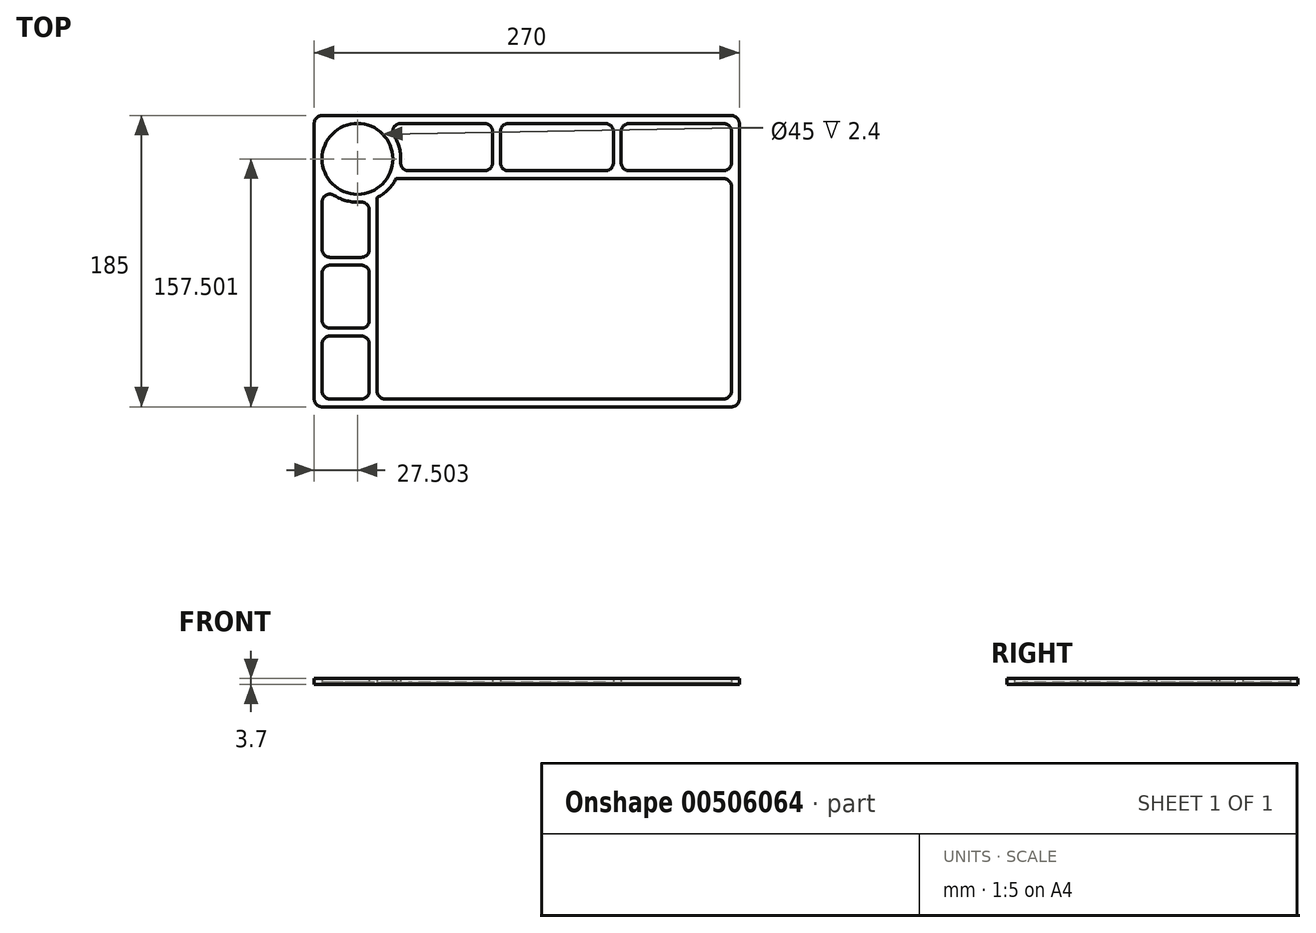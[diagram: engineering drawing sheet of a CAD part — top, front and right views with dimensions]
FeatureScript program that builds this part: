
annotation { "Feature Type Name" : "Feature", "Feature Type Description" : "" }
export const myFeature = defineFeature(function(context is Context, id is Id, definition is map)
    precondition{}
    {
        {
            var Q0;
            Q0=qCreatedBy(makeId("Top.planeOp"),FACE);
            var sketch = newSketch(context, id + "F0", { "sketchPlane" : qUnion([Q0])});
            skLineSegment(sketch, "E0.bottom", {"start": v(-130.88, 121.5) * mm, "end": v(129.12, 121.5) * mm});
            skLineSegment(sketch, "E0.top", {"start": v(-130.88, -63.5) * mm, "end": v(129.12, -63.5) * mm});
            skLineSegment(sketch, "E0.left", {"start": v(-135.88, 116.5) * mm, "end": v(-135.88, -58.5) * mm});
            skLineSegment(sketch, "E0.right", {"start": v(134.12, 116.5) * mm, "end": v(134.12, -58.5) * mm});
            skCircle(sketch, "E1", {"center": v(-108.38, 94) * mm, "radius": 22.5 * mm});
            skPoint(sketch, "E2.visualSharp", {"position": v(134.12, 121.5) * mm});
            skArc(sketch, "E2.filletArc", {"start": v(134.12, 116.5) * mm, "mid": v(132.66, 120.03) * mm, "end": v(129.12, 121.5) * mm});
            skPoint(sketch, "E3.visualSharp", {"position": v(-135.88, 121.5) * mm});
            skArc(sketch, "E3.filletArc", {"start": v(-130.88, 121.5) * mm, "mid": v(-134.41, 120.03) * mm, "end": v(-135.88, 116.5) * mm});
            skPoint(sketch, "E4.visualSharp", {"position": v(-135.88, -63.5) * mm});
            skArc(sketch, "E4.filletArc", {"start": v(-135.88, -58.5) * mm, "mid": v(-134.41, -62.04) * mm, "end": v(-130.88, -63.5) * mm});
            skPoint(sketch, "E5.visualSharp", {"position": v(134.12, -63.5) * mm});
            skArc(sketch, "E5.filletArc", {"start": v(129.12, -63.5) * mm, "mid": v(132.66, -62.04) * mm, "end": v(134.12, -58.5) * mm});
            skLineSegment(sketch, "E6", {"start": v(129.12, -58.5) * mm, "end": v(-95.88, -58.5) * mm, "construction": true});
            skArc(sketch, "E7", {"start": v(-81.92, 86.5) * mm, "mid": v(-82.46, 103.19) * mm, "end": v(-92.57, 116.5) * mm});
            skLineSegment(sketch, "E8", {"start": v(-92.57, 116.5) * mm, "end": v(-22.57, 116.5) * mm});
            skLineSegment(sketch, "E9", {"start": v(-22.57, 116.5) * mm, "end": v(-22.57, 86.5) * mm});
            skLineSegment(sketch, "E10", {"start": v(-22.57, 86.5) * mm, "end": v(-81.92, 86.5) * mm});
            skLineSegment(sketch, "E11.bottom", {"start": v(-23.62, 116.5) * mm, "end": v(-22.57, 116.5) * mm});
            skLineSegment(sketch, "E11.top", {"start": v(-23.62, 86.5) * mm, "end": v(-22.57, 86.5) * mm});
            skLineSegment(sketch, "E12", {"start": v(12.15, 86.5) * mm, "end": v(54.12, 86.5) * mm});
            skLineSegment(sketch, "E13", {"start": v(129.12, 86.5) * mm, "end": v(129.12, 116.5) * mm});
            skLineSegment(sketch, "E14", {"start": v(129.12, 116.5) * mm, "end": v(59.12, 116.5) * mm});
            skLineSegment(sketch, "E15", {"start": v(59.12, 116.5) * mm, "end": v(59.12, 86.5) * mm});
            skLineSegment(sketch, "E16", {"start": v(129.12, 116.5) * mm, "end": v(129.12, 86.5) * mm, "construction": true});
            skLineSegment(sketch, "E17", {"start": v(-83.88, 81.5) * mm, "end": v(129.12, 81.5) * mm});
            skLineSegment(sketch, "E18", {"start": v(129.12, 81.5) * mm, "end": v(129.12, -58.5) * mm});
            skLineSegment(sketch, "E19", {"start": v(-95.88, -58.5) * mm, "end": v(-95.88, 69.5) * mm});
            skArc(sketch, "E20.trimOffspring", {"start": v(-130.88, 78.18) * mm, "mid": v(-117.57, 68.07) * mm, "end": v(-100.88, 67.53) * mm});
            skLineSegment(sketch, "E21.trimOffspring", {"start": v(-92.57, 116.5) * mm, "end": v(-22.57, 116.5) * mm, "construction": true});
            skLineSegment(sketch, "E22.trimOffspring", {"start": v(-81.92, 86.5) * mm, "end": v(-22.57, 86.5) * mm, "construction": true});
            skLineSegment(sketch, "E23.trimOffspring", {"start": v(-23.62, 116.5) * mm, "end": v(-22.57, 116.5) * mm, "construction": true});
            skLineSegment(sketch, "E24.trimOffspring", {"start": v(-23.62, 86.5) * mm, "end": v(-22.57, 86.5) * mm, "construction": true});
            skLineSegment(sketch, "E25.trimOffspring", {"start": v(-83.88, 81.5) * mm, "end": v(129.12, 81.5) * mm, "construction": true});
            skLineSegment(sketch, "E26.trimOffspring", {"start": v(-95.88, 69.5) * mm, "end": v(-95.88, -58.5) * mm, "construction": true});
            skLineSegment(sketch, "E27.trimOffspring", {"start": v(-100.88, 67.53) * mm, "end": v(-100.88, 31.5) * mm, "construction": true});
            skLineSegment(sketch, "E28", {"start": v(-130.88, 78.18) * mm, "end": v(-130.88, 31.5) * mm});
            skLineSegment(sketch, "E29", {"start": v(-100.88, -58.5) * mm, "end": v(-100.88, -18.5) * mm});
            skArc(sketch, "E30.trimOffspring", {"start": v(-95.88, 69.5) * mm, "mid": v(-88.93, 74.55) * mm, "end": v(-83.88, 81.5) * mm});
            skLineSegment(sketch, "E31.trimOffspring", {"start": v(-130.88, 78.18) * mm, "end": v(-130.88, 31.5) * mm, "construction": true});
            skLineSegment(sketch, "E32", {"start": v(-95.88, -58.5) * mm, "end": v(129.12, -58.5) * mm});
            skLineSegment(sketch, "E33", {"start": v(-130.88, -58.5) * mm, "end": v(-100.88, -58.5) * mm});
            skPoint(sketch, "E34.end.orphan", {"position": v(12.15, 86.5) * mm});
            skLineSegment(sketch, "E35.trimOffspring", {"start": v(12.15, 86.5) * mm, "end": v(54.12, 86.5) * mm, "construction": true});
            skLineSegment(sketch, "E36", {"start": v(-17.57, 116.5) * mm, "end": v(-17.57, 86.5) * mm});
            skLineSegment(sketch, "E37", {"start": v(54.12, 116.5) * mm, "end": v(54.12, 86.5) * mm});
            skLineSegment(sketch, "E38.trimOffspring", {"start": v(-17.57, 116.5) * mm, "end": v(54.12, 116.5) * mm, "construction": true});
            skLineSegment(sketch, "E39.trimOffspring", {"start": v(59.12, 86.5) * mm, "end": v(129.12, 86.5) * mm, "construction": true});
            skLineSegment(sketch, "E40.trimOffspring", {"start": v(59.12, 116.5) * mm, "end": v(129.12, 116.5) * mm, "construction": true});
            skPoint(sketch, "E41.orphan", {"position": v(-20.88, 116.5) * mm});
            skLineSegment(sketch, "E42.trimOffspring", {"start": v(54.12, 116.5) * mm, "end": v(-17.57, 116.5) * mm});
            skLineSegment(sketch, "E43.trimOffspring", {"start": v(59.12, 86.5) * mm, "end": v(129.12, 86.5) * mm});
            skPoint(sketch, "E44.orphan", {"position": v(-20.88, 86.5) * mm});
            skLineSegment(sketch, "E45", {"start": v(12.15, 86.5) * mm, "end": v(-17.57, 86.5) * mm});
            skLineSegment(sketch, "E46", {"start": v(-130.88, -18.5) * mm, "end": v(-100.88, -18.5) * mm});
            skLineSegment(sketch, "E47", {"start": v(-100.88, -13.5) * mm, "end": v(-130.88, -13.5) * mm});
            skLineSegment(sketch, "E48", {"start": v(-100.88, 26.5) * mm, "end": v(-130.88, 26.5) * mm});
            skLineSegment(sketch, "E49", {"start": v(-100.88, 31.5) * mm, "end": v(-130.88, 31.5) * mm});
            skLineSegment(sketch, "E50.trimOffspring", {"start": v(-130.88, 26.5) * mm, "end": v(-130.88, -13.5) * mm, "construction": true});
            skLineSegment(sketch, "E51.trimOffspring", {"start": v(-100.88, 26.5) * mm, "end": v(-100.88, -13.5) * mm, "construction": true});
            skLineSegment(sketch, "E52.trimOffspring", {"start": v(-100.88, -18.5) * mm, "end": v(-100.88, -58.5) * mm, "construction": true});
            skLineSegment(sketch, "E53.trimOffspring", {"start": v(-130.88, -18.5) * mm, "end": v(-130.88, -58.5) * mm, "construction": true});
            skLineSegment(sketch, "E54.trimOffspring", {"start": v(-100.88, -13.5) * mm, "end": v(-100.88, 26.5) * mm});
            skLineSegment(sketch, "E55.trimOffspring", {"start": v(-100.88, 31.5) * mm, "end": v(-100.88, 67.53) * mm});
            skLineSegment(sketch, "E56.trimOffspring", {"start": v(-130.88, 26.5) * mm, "end": v(-130.88, -13.5) * mm});
            skLineSegment(sketch, "E57.trimOffspring", {"start": v(-130.88, -18.5) * mm, "end": v(-130.88, -58.5) * mm});
            skPoint(sketch, "E58.orphan", {"position": v(-135.88, 86.5) * mm});
            skPoint(sketch, "E59.start.orphan", {"position": v(-135.88, 81.5) * mm});
            skPoint(sketch, "E60.orphan", {"position": v(-95.88, 121.5) * mm});
            skPoint(sketch, "E61.orphan", {"position": v(-100.88, 121.5) * mm});
            skPoint(sketch, "E62.orphan", {"position": v(129.12, 121.5) * mm});
            skLineSegment(sketch, "E63.trimOffspring", {"start": v(129.12, 81.5) * mm, "end": v(129.12, -58.5) * mm, "construction": true});
            skPoint(sketch, "E64.orphan", {"position": v(129.12, -63.5) * mm});
            skSolve(sketch);
        }
        {
            var Q0;
            Q0=makeQuery(id+"F0.imprint","IMPRINT",FACE,{"disambiguationData":[TD([[makeQuery(id+"F0.imprint","IMPRINT",EDGE,{"derivedFrom":sQuery(id+"F0.wireOp",EDGE,"E0.bottom")}),-1.0]])]});
            extrude(context, id + "F1", {"entities" : qUnion([Q0]), "depth" : 3.7 * mm, "offsetDistance" : 25 * mm});
        }
        {
            var Q0;
            Q0=makeQuery(id+"F0.imprint","IMPRINT",FACE,{"disambiguationData":[TD([[makeQuery(id+"F0.imprint","IMPRINT",EDGE,{"derivedFrom":sQuery(id+"F0.wireOp",EDGE,"E0.bottom")}),-1.0]])]});
            var Q1;
            Q1=makeQuery(id+"F0.imprint","IMPRINT",FACE,{"disambiguationData":[TD([[makeQuery(id+"F0.imprint","IMPRINT",EDGE,{"derivedFrom":sQuery(id+"F0.wireOp",EDGE,"E17")}),-1.0]])]});
            var Q2;
            Q2=makeQuery(id+"F0.imprint","IMPRINT",FACE,{"disambiguationData":[TD([[makeQuery(id+"F0.imprint","IMPRINT",EDGE,{"derivedFrom":sQuery(id+"F0.wireOp",EDGE,"E13")}),1.0]])]});
            var Q3;
            Q3=makeQuery(id+"F0.imprint","IMPRINT",FACE,{"disambiguationData":[TD([[makeQuery(id+"F0.imprint","IMPRINT",EDGE,{"derivedFrom":sQuery(id+"F0.wireOp",EDGE,"E12")}),1.0]])]});
            var Q4;
            Q4=makeQuery(id+"F0.imprint","IMPRINT",FACE,{"disambiguationData":[TD([[makeQuery(id+"F0.imprint","IMPRINT",EDGE,{"derivedFrom":sQuery(id+"F0.wireOp",EDGE,"E7")}),-1.0]])]});
            var Q5;
            Q5=makeQuery(id+"F0.imprint","IMPRINT",FACE,{"disambiguationData":[TD([[makeQuery(id+"F0.imprint","IMPRINT",EDGE,{"derivedFrom":sQuery(id+"F0.wireOp",EDGE,"E1")}),1.0]])]});
            var Q6;
            Q6=makeQuery(id+"F0.imprint","IMPRINT",FACE,{"disambiguationData":[TD([[makeQuery(id+"F0.imprint","IMPRINT",EDGE,{"derivedFrom":sQuery(id+"F0.wireOp",EDGE,"E20.trimOffspring")}),-1.0]])]});
            var Q7;
            Q7=makeQuery(id+"F0.imprint","IMPRINT",FACE,{"disambiguationData":[TD([[makeQuery(id+"F0.imprint","IMPRINT",EDGE,{"derivedFrom":sQuery(id+"F0.wireOp",EDGE,"E47")}),-1.0]])]});
            var Q8;
            Q8=makeQuery(id+"F0.imprint","IMPRINT",FACE,{"disambiguationData":[TD([[makeQuery(id+"F0.imprint","IMPRINT",EDGE,{"derivedFrom":sQuery(id+"F0.wireOp",EDGE,"E29")}),1.0]])]});
            extrude(context, id + "F2", {"entities" : qUnion([Q0, Q1, Q2, Q3, Q4, Q5, Q6, Q7, Q8]), "operationType" : NewBodyOperationType.ADD, "depth" : 1.3 * mm, "offsetDistance" : 25 * mm});
        }
        {
            var Q0;
            Q0=makeQuery(id+"F1.opExtrude","SWEPT_EDGE",EDGE,{"disambiguationData":[OSD([sQuery(id+"F0.wireOp",EDGE,"E14"),sQuery(id+"F0.wireOp",EDGE,"E15")])]});
            var Q1;
            Q1=makeQuery(id+"F1.opExtrude","SWEPT_EDGE",EDGE,{"disambiguationData":[OSD([sQuery(id+"F0.wireOp",EDGE,"E17"),sQuery(id+"F0.wireOp",EDGE,"E18")])]});
            var Q2;
            Q2=makeQuery(id+"F1.opExtrude","SWEPT_EDGE",EDGE,{"disambiguationData":[OSD([sQuery(id+"F0.wireOp",EDGE,"E13"),sQuery(id+"F0.wireOp",EDGE,"E14")])]});
            var Q3;
            Q3=makeQuery(id+"F1.opExtrude","SWEPT_EDGE",EDGE,{"disambiguationData":[OSD([sQuery(id+"F0.wireOp",EDGE,"E13"),sQuery(id+"F0.wireOp",EDGE,"E43.trimOffspring")])]});
            var Q4;
            Q4=makeQuery(id+"F1.opExtrude","SWEPT_EDGE",EDGE,{"disambiguationData":[OSD([sQuery(id+"F0.wireOp",EDGE,"E15"),sQuery(id+"F0.wireOp",EDGE,"E43.trimOffspring")])]});
            var Q5;
            Q5=makeQuery(id+"F1.opExtrude","SWEPT_EDGE",EDGE,{"disambiguationData":[OSD([sQuery(id+"F0.wireOp",EDGE,"E12"),sQuery(id+"F0.wireOp",EDGE,"E37")])]});
            var Q6;
            Q6=makeQuery(id+"F1.opExtrude","SWEPT_EDGE",EDGE,{"disambiguationData":[OSD([sQuery(id+"F0.wireOp",EDGE,"E37"),sQuery(id+"F0.wireOp",EDGE,"E42.trimOffspring")])]});
            var Q7;
            Q7=makeQuery(id+"F1.opExtrude","SWEPT_EDGE",EDGE,{"disambiguationData":[OSD([sQuery(id+"F0.wireOp",EDGE,"E36"),sQuery(id+"F0.wireOp",EDGE,"E45")])]});
            var Q8;
            Q8=makeQuery(id+"F1.opExtrude","SWEPT_EDGE",EDGE,{"disambiguationData":[OSD([sQuery(id+"F0.wireOp",EDGE,"E7"),sQuery(id+"F0.wireOp",EDGE,"E10")])]});
            var Q9;
            Q9=makeQuery(id+"F1.opExtrude","SWEPT_EDGE",EDGE,{"disambiguationData":[OSD([sQuery(id+"F0.wireOp",EDGE,"E47"),sQuery(id+"F0.wireOp",EDGE,"E56.trimOffspring")])]});
            var Q10;
            Q10=makeQuery(id+"F1.opExtrude","SWEPT_EDGE",EDGE,{"disambiguationData":[OSD([sQuery(id+"F0.wireOp",EDGE,"E48"),sQuery(id+"F0.wireOp",EDGE,"E54.trimOffspring")])]});
            var Q11;
            Q11=makeQuery(id+"F1.opExtrude","SWEPT_EDGE",EDGE,{"disambiguationData":[OSD([sQuery(id+"F0.wireOp",EDGE,"E20.trimOffspring"),sQuery(id+"F0.wireOp",EDGE,"E55.trimOffspring")])]});
            var Q12;
            Q12=makeQuery(id+"F1.opExtrude","SWEPT_EDGE",EDGE,{"disambiguationData":[OSD([sQuery(id+"F0.wireOp",EDGE,"E29"),sQuery(id+"F0.wireOp",EDGE,"E46")])]});
            var Q13;
            Q13=makeQuery(id+"F1.opExtrude","SWEPT_EDGE",EDGE,{"disambiguationData":[OSD([sQuery(id+"F0.wireOp",EDGE,"E48"),sQuery(id+"F0.wireOp",EDGE,"E56.trimOffspring")])]});
            var Q14;
            Q14=makeQuery(id+"F1.opExtrude","SWEPT_EDGE",EDGE,{"disambiguationData":[OSD([sQuery(id+"F0.wireOp",EDGE,"E20.trimOffspring"),sQuery(id+"F0.wireOp",EDGE,"E28")])]});
            var Q15;
            Q15=makeQuery(id+"F1.opExtrude","SWEPT_EDGE",EDGE,{"disambiguationData":[OSD([sQuery(id+"F0.wireOp",EDGE,"E7"),sQuery(id+"F0.wireOp",EDGE,"E8")])]});
            var Q16;
            Q16=makeQuery(id+"F1.opExtrude","SWEPT_EDGE",EDGE,{"disambiguationData":[OSD([sQuery(id+"F0.wireOp",EDGE,"E36"),sQuery(id+"F0.wireOp",EDGE,"E42.trimOffspring")])]});
            var Q17;
            Q17=makeQuery(id+"F1.opExtrude","SWEPT_EDGE",EDGE,{"disambiguationData":[OSD([sQuery(id+"F0.wireOp",EDGE,"E33"),sQuery(id+"F0.wireOp",EDGE,"E57.trimOffspring")])]});
            var Q18;
            Q18=makeQuery(id+"F1.opExtrude","SWEPT_EDGE",EDGE,{"disambiguationData":[OSD([sQuery(id+"F0.wireOp",EDGE,"E28"),sQuery(id+"F0.wireOp",EDGE,"E49")])]});
            var Q19;
            Q19=makeQuery(id+"F1.opExtrude","SWEPT_EDGE",EDGE,{"disambiguationData":[OSD([sQuery(id+"F0.wireOp",EDGE,"E47"),sQuery(id+"F0.wireOp",EDGE,"E54.trimOffspring")])]});
            var Q20;
            Q20=makeQuery(id+"F1.opExtrude","SWEPT_EDGE",EDGE,{"disambiguationData":[OSD([sQuery(id+"F0.wireOp",EDGE,"E49"),sQuery(id+"F0.wireOp",EDGE,"E55.trimOffspring")])]});
            var Q21;
            Q21=makeQuery(id+"F1.opExtrude","SWEPT_EDGE",EDGE,{"disambiguationData":[OSD([sQuery(id+"F0.wireOp",EDGE,"E29"),sQuery(id+"F0.wireOp",EDGE,"E33")])]});
            var Q22;
            Q22=makeQuery(id+"F1.opExtrude","SWEPT_EDGE",EDGE,{"disambiguationData":[OSD([sQuery(id+"F0.wireOp",EDGE,"E19"),sQuery(id+"F0.wireOp",EDGE,"E32")])]});
            var Q23;
            Q23=makeQuery(id+"F1.opExtrude","SWEPT_EDGE",EDGE,{"disambiguationData":[OSD([sQuery(id+"F0.wireOp",EDGE,"E46"),sQuery(id+"F0.wireOp",EDGE,"E57.trimOffspring")])]});
            var Q24;
            Q24=makeQuery(id+"F1.opExtrude","SWEPT_EDGE",EDGE,{"disambiguationData":[OSD([sQuery(id+"F0.wireOp",EDGE,"E18"),sQuery(id+"F0.wireOp",EDGE,"E32")])]});
            var Q25;
            Q25=makeQuery(id+"F1.opExtrude","SWEPT_EDGE",EDGE,{"disambiguationData":[OSD([sQuery(id+"F0.wireOp",EDGE,"E9"),sQuery(id+"F0.wireOp",EDGE,"E11.top")])]});
            var Q26;
            Q26=makeQuery(id+"F1.opExtrude","SWEPT_EDGE",EDGE,{"disambiguationData":[OSD([sQuery(id+"F0.wireOp",EDGE,"E9"),sQuery(id+"F0.wireOp",EDGE,"E11.bottom")])]});
            fillet(context, id + "F3", {"entities" : qUnion([Q0, Q1, Q2, Q3, Q4, Q5, Q6, Q7, Q8, Q9, Q10, Q11, Q12, Q13, Q14, Q15, Q16, Q17, Q18, Q19, Q20, Q21, Q22, Q23, Q24, Q25, Q26]), "radius" : 5 * mm, "tangentPropagation" : true, "allowEdgeOverflow" : false});
        }
    });
